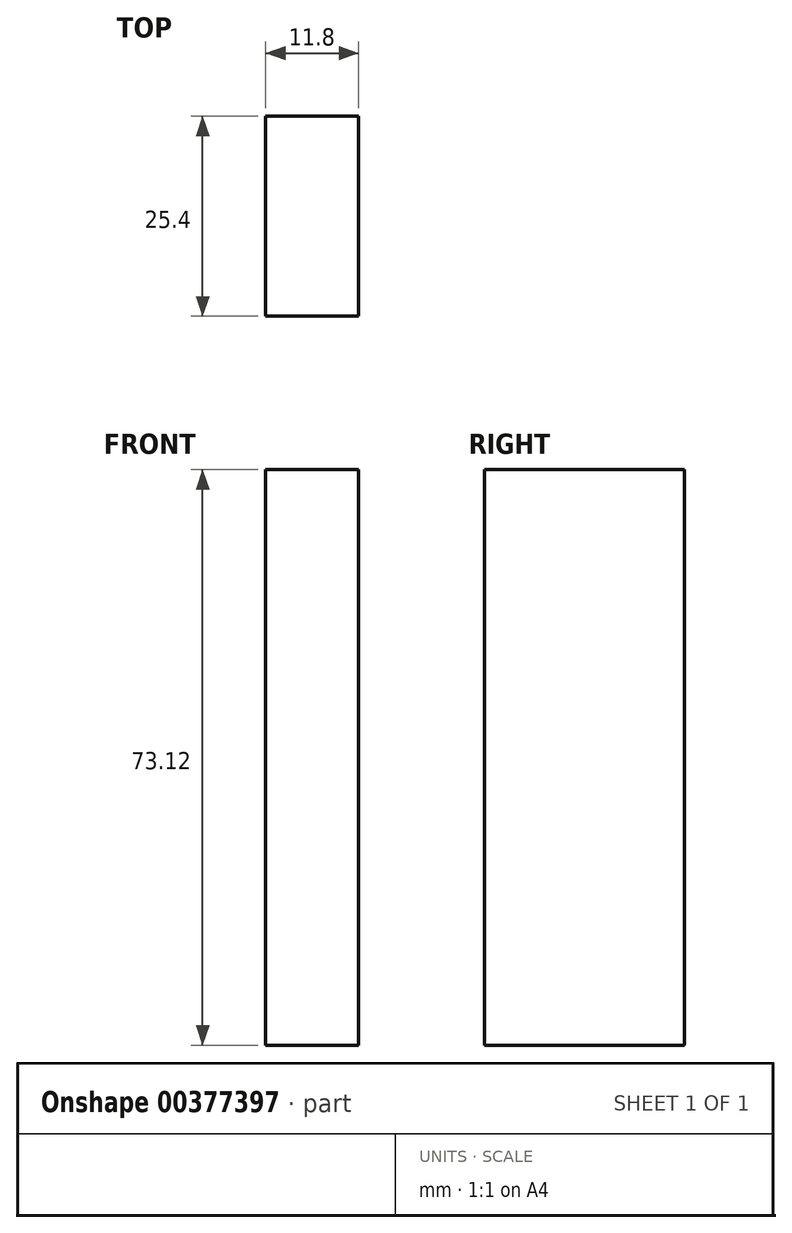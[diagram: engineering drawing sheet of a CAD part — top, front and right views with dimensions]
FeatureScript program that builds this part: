
annotation { "Feature Type Name" : "Feature", "Feature Type Description" : "" }
export const myFeature = defineFeature(function(context is Context, id is Id, definition is map)
    precondition{}
    {
        {
            var Q0;
            Q0=qCreatedBy(makeId("Front.planeOp"),FACE);
            var sketch = newSketch(context, id + "F0", { "sketchPlane" : qUnion([Q0])});
            skLineSegment(sketch, "E0.bottom", {"start": v(-5.9, 36.56) * mm, "end": v(5.9, 36.56) * mm});
            skLineSegment(sketch, "E0.top", {"start": v(-5.9, -36.56) * mm, "end": v(5.9, -36.56) * mm});
            skLineSegment(sketch, "E0.left", {"start": v(-5.9, 36.56) * mm, "end": v(-5.9, -36.56) * mm});
            skLineSegment(sketch, "E0.right", {"start": v(5.9, 36.56) * mm, "end": v(5.9, -36.56) * mm});
            skPoint(sketch, "E0.middle", {"position": v(0, 0) * mm});
            skSolve(sketch);
        }
        {
            var Q0;
            Q0 = qSketchRegion(id + "F0", true);
            extrude(context, id + "F1", {"entities" : qUnion([Q0]), "depth" : 25.4 * mm});
        }
    });
